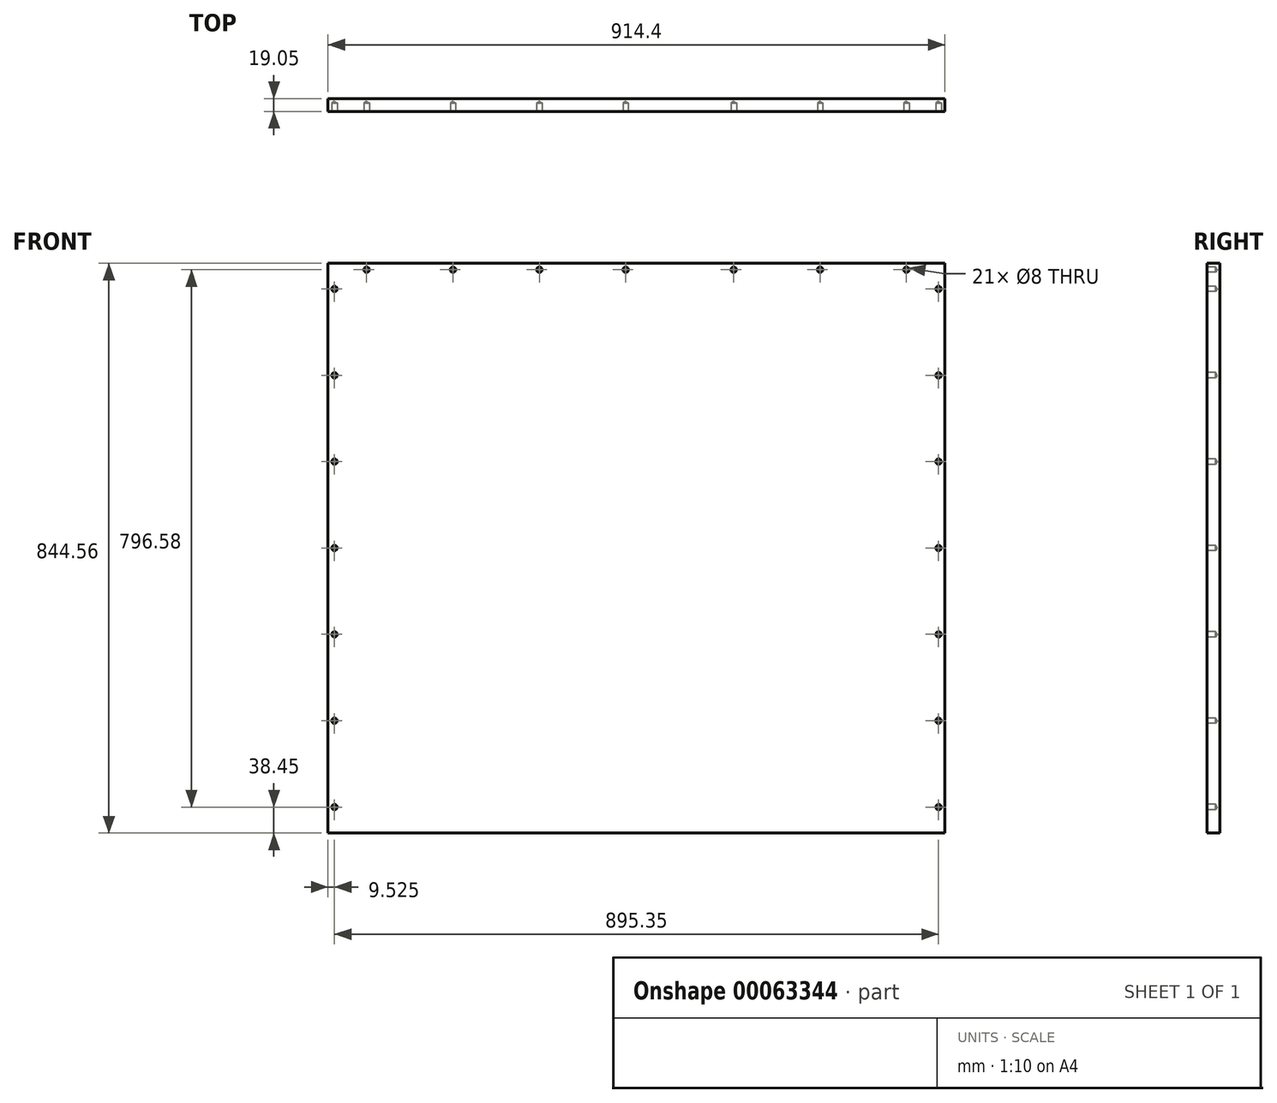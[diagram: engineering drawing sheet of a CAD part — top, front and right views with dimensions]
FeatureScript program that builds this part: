
annotation { "Feature Type Name" : "Feature", "Feature Type Description" : "" }
export const myFeature = defineFeature(function(context is Context, id is Id, definition is map)
    precondition{}
    {
        {
            var Q0;
            Q0=qCreatedBy(makeId("Front.planeOp"),FACE);
            var sketch = newSketch(context, id + "F0", { "sketchPlane" : qUnion([Q0])});
            skLineSegment(sketch, "E0.rect.bottom", {"start": v(457.2, -422.27) * mm, "end": v(-457.2, -422.28) * mm});
            skLineSegment(sketch, "E0.rect.top", {"start": v(457.2, 422.28) * mm, "end": v(-457.2, 422.27) * mm});
            skLineSegment(sketch, "E0.rect.left", {"start": v(457.2, -422.27) * mm, "end": v(457.2, 422.28) * mm});
            skLineSegment(sketch, "E0.rect.right", {"start": v(-457.2, -422.27) * mm, "end": v(-457.2, 422.27) * mm});
            skPoint(sketch, "E0.rect.middle", {"position": v(0, 0) * mm});
            skSolve(sketch);
        }
        {
            var Q0;
            Q0=makeQuery(id+"F0.imprint","IMPRINT",FACE,{"disambiguationData":[TD([[makeQuery(id+"F0.imprint","IMPRINT",EDGE,{"derivedFrom":sQuery(id+"F0.wireOp",EDGE,"E0.rect.bottom")}),-1.0]])]});
            extrude(context, id + "F1", {"entities" : qUnion([Q0]), "oppositeDirection" : true, "depth" : 19.05 * mm});
        }
        {
            var Q0;
            Q0=makeQuery(id+"F1.opExtrude","CAP_FACE",FACE,{"disambiguationData":[OSD([sQuery(id+"F0.wireOp",EDGE,"E0.rect.bottom"),sQuery(id+"F0.wireOp",EDGE,"E0.rect.top"),sQuery(id+"F0.wireOp",EDGE,"E0.rect.left"),sQuery(id+"F0.wireOp",EDGE,"E0.rect.right")])],"isStart":true});
            var sketch = newSketch(context, id + "F2", { "sketchPlane" : qUnion([Q0])});
            skPoint(sketch, "E1", {"position": v(-447.68, 384.17) * mm});
            skPoint(sketch, "E2", {"position": v(-447.68, 256.17) * mm});
            skPoint(sketch, "E3", {"position": v(-447.68, 128.17) * mm});
            skPoint(sketch, "E4", {"position": v(-447.68, 0.17) * mm});
            skPoint(sketch, "E5", {"position": v(-447.68, -127.83) * mm});
            skPoint(sketch, "E6", {"position": v(-447.68, -255.83) * mm});
            skPoint(sketch, "E7", {"position": v(-447.68, -383.83) * mm});
            skLineSegment(sketch, "E8", {"start": v(0, -422.27) * mm, "end": v(0, 422.27) * mm, "construction": true});
            skPoint(sketch, "E9.MirrorP", {"position": v(447.68, 384.17) * mm});
            skPoint(sketch, "E10.MirrorP", {"position": v(447.68, 256.17) * mm});
            skPoint(sketch, "E11.MirrorP", {"position": v(447.68, 128.17) * mm});
            skPoint(sketch, "E12.MirrorP", {"position": v(447.68, 0.17) * mm});
            skPoint(sketch, "E13.MirrorP", {"position": v(447.68, -127.83) * mm});
            skPoint(sketch, "E14.MirrorP", {"position": v(447.68, -255.83) * mm});
            skPoint(sketch, "E15.MirrorP", {"position": v(447.67, -383.83) * mm});
            skPoint(sketch, "E16", {"position": v(-400.05, 412.75) * mm});
            skPoint(sketch, "E17", {"position": v(-272.05, 412.75) * mm});
            skPoint(sketch, "E18", {"position": v(-144.05, 412.75) * mm});
            skPoint(sketch, "E19.MirrorP", {"position": v(400.05, 412.75) * mm});
            skPoint(sketch, "E20.MirrorP", {"position": v(272.05, 412.75) * mm});
            skPoint(sketch, "E21.MirrorP", {"position": v(144.05, 412.75) * mm});
            skPoint(sketch, "E22", {"position": v(-16.05, 412.75) * mm});
            skSolve(sketch);
        }
        {
            var Q0;
            Q0=sQuery(id+"F2.wireOp",VERTEX,"E7");
            var Q1;
            Q1=sQuery(id+"F2.wireOp",VERTEX,"E6");
            var Q2;
            Q2=sQuery(id+"F2.wireOp",VERTEX,"E5");
            var Q3;
            Q3=sQuery(id+"F2.wireOp",VERTEX,"E4");
            var Q4;
            Q4=sQuery(id+"F2.wireOp",VERTEX,"E3");
            var Q5;
            Q5=sQuery(id+"F2.wireOp",VERTEX,"E2");
            var Q6;
            Q6=sQuery(id+"F2.wireOp",VERTEX,"E1");
            var Q7;
            Q7=sQuery(id+"F2.wireOp",VERTEX,"E16");
            var Q8;
            Q8=sQuery(id+"F2.wireOp",VERTEX,"E17");
            var Q9;
            Q9=sQuery(id+"F2.wireOp",VERTEX,"E18");
            var Q10;
            Q10=sQuery(id+"F2.wireOp",VERTEX,"E22");
            var Q11;
            Q11=sQuery(id+"F2.wireOp",VERTEX,"E21.MirrorP");
            var Q12;
            Q12=sQuery(id+"F2.wireOp",VERTEX,"E20.MirrorP");
            var Q13;
            Q13=sQuery(id+"F2.wireOp",VERTEX,"E19.MirrorP");
            var Q14;
            Q14=sQuery(id+"F2.wireOp",VERTEX,"E9.MirrorP");
            var Q15;
            Q15=sQuery(id+"F2.wireOp",VERTEX,"E10.MirrorP");
            var Q16;
            Q16=sQuery(id+"F2.wireOp",VERTEX,"E11.MirrorP");
            var Q17;
            Q17=sQuery(id+"F2.wireOp",VERTEX,"E12.MirrorP");
            var Q18;
            Q18=sQuery(id+"F2.wireOp",VERTEX,"E13.MirrorP");
            var Q19;
            Q19=sQuery(id+"F2.wireOp",VERTEX,"E14.MirrorP");
            var Q20;
            Q20=sQuery(id+"F2.wireOp",VERTEX,"E15.MirrorP");
            var Q21;
            Q21=makeQuery(id+"F1.opExtrude","SWEPT_BODY",BODY,{"disambiguationData":[OSD([sQuery(id+"F0.wireOp",EDGE,"E0.rect.bottom"),sQuery(id+"F0.wireOp",EDGE,"E0.rect.top"),sQuery(id+"F0.wireOp",EDGE,"E0.rect.left"),sQuery(id+"F0.wireOp",EDGE,"E0.rect.right")])]});
            hole(context, id + "F3", {"style" : HoleStyle.SIMPLE, "holeDiameter" : 8 * mm, "endStyle" : HoleEndStyle.BLIND, "holeDepth" : 12.7 * mm, "locations" : qUnion([Q0, Q1, Q2, Q3, Q4, Q5, Q6, Q7, Q8, Q9, Q10, Q11, Q12, Q13, Q14, Q15, Q16, Q17, Q18, Q19, Q20]), "scope" : qUnion([Q21])});
        }
    });
